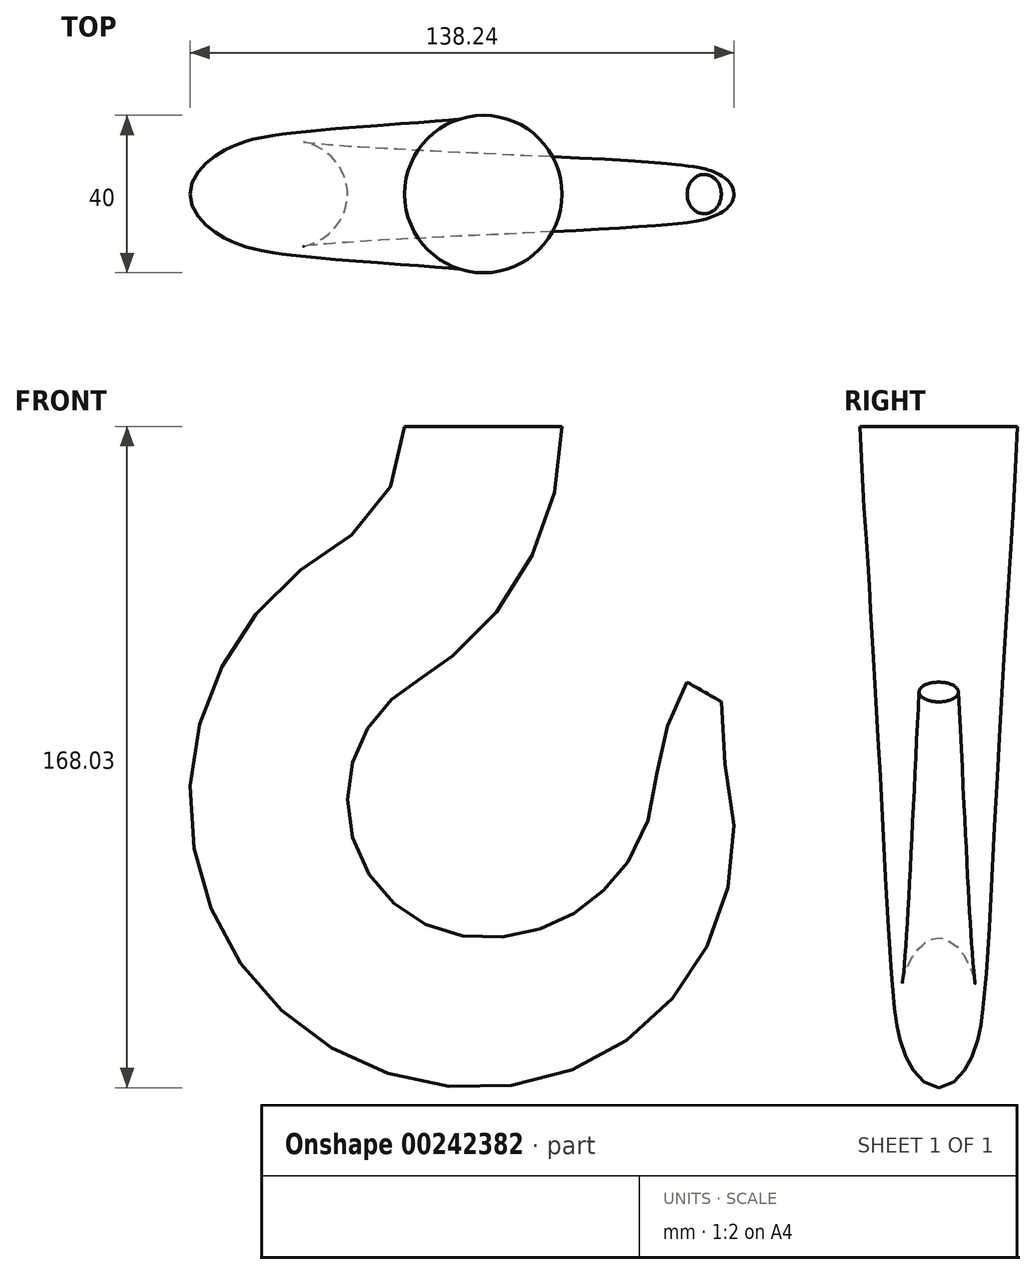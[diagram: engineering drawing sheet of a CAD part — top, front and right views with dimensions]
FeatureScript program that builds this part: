
annotation { "Feature Type Name" : "Feature", "Feature Type Description" : "" }
export const myFeature = defineFeature(function(context is Context, id is Id, definition is map)
    precondition{}
    {
        {
            var Q0;
            Q0=qCreatedBy(makeId("Front.planeOp"),FACE);
            var sketch = newSketch(context, id + "F0", { "sketchPlane" : qUnion([Q0])});
            skLineSegment(sketch, "E0", {"start": v(-20.45, 95) * mm, "end": v(19.55, 95) * mm});
            skArc(sketch, "E1", {"start": v(-37.8, 64.77) * mm, "mid": v(-25.1, 77.57) * mm, "end": v(-20.45, 95) * mm});
            skArc(sketch, "E2", {"start": v(-17.64, 30.23) * mm, "mid": v(9.59, 57.65) * mm, "end": v(19.55, 95) * mm});
            skArc(sketch, "E3", {"start": v(-37.8, 64.77) * mm, "mid": v(-65.04, 37.35) * mm, "end": v(-75, 0) * mm});
            skArc(sketch, "E4", {"start": v(-35, 0) * mm, "mid": v(-24.75, -24.75) * mm, "end": v(0, -35) * mm});
            skArc(sketch, "E5", {"start": v(-17.64, 30.23) * mm, "mid": v(-30.35, 17.43) * mm, "end": v(-35, 0) * mm});
            skLineSegment(sketch, "E6", {"start": v(81.09, 0) * mm, "end": v(-211.2, 0) * mm, "construction": true});
            skArc(sketch, "E7", {"start": v(61.27, 7.87) * mm, "mid": v(50.05, -47.27) * mm, "end": v(0, -73) * mm});
            skArc(sketch, "E8", {"start": v(43.5, 5) * mm, "mid": v(46.04, 17.94) * mm, "end": v(51.33, 30) * mm});
            skLineSegment(sketch, "E9", {"start": v(51.33, 30) * mm, "end": v(60, 25) * mm});
            skArc(sketch, "E10", {"start": v(60, 25) * mm, "mid": v(59.89, 16.38) * mm, "end": v(61.27, 7.87) * mm});
            skArc(sketch, "E11", {"start": v(0, -35) * mm, "mid": v(29.55, -23.48) * mm, "end": v(43.5, 5) * mm});
            skArc(sketch, "E12", {"start": v(-75, 0) * mm, "mid": v(-52.9, -52.33) * mm, "end": v(0, -73) * mm});
            skCircle(sketch, "E13", {"center": v(55.66, 27.5) * mm, "radius": 5 * mm, "construction": true});
            skSolve(sketch);
        }
        {
            var Q0;
            Q0=sQuery(id+"F0.wireOp",EDGE,"E0");
            cPoint(context, id + "F1", {"entities" : qUnion([Q0]), "parameter" : 0.5});
        }
        {
            var Q0;
            Q0=qCreatedBy(makeId("Top.planeOp"),FACE);
            var Q1;
            Q1 = qCreatedBy(id + "F1" ,VERTEX);
            cPlane(context, id + "F2", {"entities" : qUnion([Q0, Q1]), "cplaneType" : CPlaneType.PLANE_POINT, "offset" : 25 * mm, "width" : 150 * mm, "height" : 150 * mm});
        }
        {
            var Q0;
            Q0=qCreatedBy(id+"F2.planeOp",FACE);
            var sketch = newSketch(context, id + "F3", { "sketchPlane" : qUnion([Q0])});
            skLineSegment(sketch, "E14.0", {"start": v(-20.45, 0) * mm, "end": v(19.55, 0) * mm, "construction": true});
            skCircle(sketch, "E15", {"center": v(-0.45, 0) * mm, "radius": 20 * mm});
            skSolve(sketch);
        }
        {
            var Q0;
            Q0=qCreatedBy(makeId("Front.planeOp"),FACE);
            var sketch = newSketch(context, id + "F4", { "sketchPlane" : qUnion([Q0])});
            skLineSegment(sketch, "E16.0", {"start": v(51.33, 30) * mm, "end": v(60, 25) * mm});
            skSolve(sketch);
        }
        {
            var Q0;
            Q0=qCreatedBy(makeId("Top.planeOp"),FACE);
            var Q1;
            Q1=sQuery(id+"F4.wireOp",EDGE,"E16.0");
            cPlane(context, id + "F5", {"entities" : qUnion([Q0, Q1]), "cplaneType" : CPlaneType.LINE_ANGLE, "offset" : 25 * mm, "angle" : 0 * degree, "width" : 150 * mm, "height" : 150 * mm});
        }
        {
            var Q0;
            Q0=qCreatedBy(id+"F5.planeOp",FACE);
            var sketch = newSketch(context, id + "F6", { "sketchPlane" : qUnion([Q0])});
            skPoint(sketch, "E17.0", {"position": v(34.45, 0) * mm});
            skCircle(sketch, "E18", {"center": v(34.45, 0) * mm, "radius": 5 * mm});
            skSolve(sketch);
        }
        {
            var Q0;
            Q0=qCreatedBy(makeId("Front.planeOp"),FACE);
            var sketch = newSketch(context, id + "F7", { "sketchPlane" : qUnion([Q0])});
            skArc(sketch, "E19.0.7", {"start": v(-20.45, 95) * mm, "mid": v(-25.1, 77.57) * mm, "end": v(-37.8, 64.77) * mm});
            skArc(sketch, "E19.0.8", {"start": v(-37.8, 64.77) * mm, "mid": v(-65.04, 37.35) * mm, "end": v(-75, 0) * mm});
            skArc(sketch, "E19.0.9", {"start": v(-75, 0) * mm, "mid": v(-52.9, -52.33) * mm, "end": v(0, -73) * mm});
            skArc(sketch, "E19.0.10", {"start": v(0, -73) * mm, "mid": v(50.05, -47.27) * mm, "end": v(61.27, 7.87) * mm});
            skArc(sketch, "E19.0.11", {"start": v(61.27, 7.87) * mm, "mid": v(59.89, 16.38) * mm, "end": v(60, 25) * mm});
            skSolve(sketch);
        }
        {
            var Q0;
            Q0=qCreatedBy(makeId("Front.planeOp"),FACE);
            var sketch = newSketch(context, id + "F8", { "sketchPlane" : qUnion([Q0])});
            skArc(sketch, "E20.0.1", {"start": v(51.33, 30) * mm, "mid": v(46.04, 17.94) * mm, "end": v(43.5, 5) * mm});
            skArc(sketch, "E20.0.2", {"start": v(43.5, 5) * mm, "mid": v(29.55, -23.48) * mm, "end": v(0, -35) * mm});
            skArc(sketch, "E20.0.3", {"start": v(0, -35) * mm, "mid": v(-24.75, -24.75) * mm, "end": v(-35, 0) * mm});
            skArc(sketch, "E20.0.4", {"start": v(-35, 0) * mm, "mid": v(-30.35, 17.43) * mm, "end": v(-17.64, 30.23) * mm});
            skArc(sketch, "E20.0.5", {"start": v(-17.64, 30.23) * mm, "mid": v(9.59, 57.65) * mm, "end": v(19.55, 95) * mm});
            skSolve(sketch);
        }
        {
            var Q0;
            Q0 = qSketchRegion(id + "F6", true);
            var Q1;
            Q1 = qSketchRegion(id + "F3", true);
            var Q2;
            Q2 = qConstructionFilter(qBodyType(qCreatedBy(id + "F7" ,EDGE), BodyType.WIRE), ConstructionObject.NO);
            var Q3;
            Q3 = qConstructionFilter(qBodyType(qCreatedBy(id + "F8" ,EDGE), BodyType.WIRE), ConstructionObject.NO);
            loft(context, id + "F9", {"addGuides" : true, "sheetProfilesArray" : [{ "sheetProfileEntities" : qUnion([Q0]) }, { "sheetProfileEntities" : qUnion([Q1]) }], "guidesArray" : [{ "guideEntities" : qUnion([Q2]), "guideDerivativeType" : LoftGuideDerivativeType.DEFAULT, "guideDerivativeMagnitude" : 1 }, { "guideEntities" : qUnion([Q3]), "guideDerivativeType" : LoftGuideDerivativeType.DEFAULT, "guideDerivativeMagnitude" : 1 }]});
        }
    });
